# Revit family: 756-106-025 DN150-1200
name_source: partatom
category: Pipe Accessories
units: mm (PartAtom-declared; Revit-internal decimal feet)

## family parameters
Always vertical = Yes
Cut with Voids When Loaded = No
Part Type = Valve - Breaks Into
Round Connector Dimension = Use Diameter
Shared = No
Work Plane-Based = No

## types (29) — shared parameters
1 = 1 mm  [stored 0.00328084 ft]
5 = 5 mm  [stored 0.0164042 ft]
D1 = 6 mm  [stored 0.019685 ft]
D1. = 6 mm  [stored 0.019685 ft]
DN1000_PN10 = 756-1000-1-04006047
 756-1000-1-04006047
 756-1000-1-04006047
756-1000-1-04006047
DN1000_PN16 = 756-1000-1-14006047
DN1200_PN10 = 756-1200-1-04006047
DN1200_PN16 = 756-1200-1-14006047
DN1400_PN10 = 756-1400-1-04006047
DN1400_PN16 = 756-1400-1-14006047
DN150_PN10/16 = 756-0150-1-14006047
DN200_PN10 = 756-0200-1-04006047
DN200_PN16 = 756-0200-1-14006047
 756-0200-1-14006047
756-0200-1-14006047
DN250_PN10 = 756-0250-1-04006047
DN250_PN16 = 756-0250-1-14006047
DN300_PN10 = 756-0300-1-04006047
756-0300-1-14006047
DN300_PN16 = 756-0300-1-14006047
DN350_PN10 = 756-0350-1-04006047
DN350_PN16 = 756-0350-1-14006047
DN400_PN10 = 756-0400-1-04006047
DN400_PN16 = 756-0400-1-14006047
DN450_PN10 = 756-0450-1-04006047
DN450_PN16 = 756-0450-1-14006047
DN500_PN10 = 756-0500-1-04006047
DN500_PN16 = 756-0500-1-14006047
DN600_PN10 = 756-0600-1-04006047
DN600_PN16 = 756-0600-1-14006047
DN700_PN10 = 756-0700-1-04006047
DN700_PN16 = 756-0700-1-14006047
DN800_PN10 = 756-0800-1-04006047
DN800_PN16 = 756-0800-1-14006047
DN900_PN10 = 756-0900-1-04006047
DN900_PN16 = 756-0900-1-14006047
Description_ = AVK DOUBLE ECCENTRIC BUTTERFLY VALVE, PN10/16
Search_table = 756-106-025 DN150-1200
URL product pages = https://www.avkvalves.com
zero-valued in all types: .5, 0, Default Elevation, Stem_dia

## per-type parameters (varying)
- DN0150_PN10/16: Bore=75 mm; DN=150 mm; FL_OD=152 mm; FL_T=19 mm  [stored 0.062336 ft]; H2=200 mm; HW=4 mm  [stored 0.0131234 ft]; Hw=8 mm  [stored 0.0262467 ft]; Inside_R=53 mm; L=105 mm; L1=1 mm  [stored 0.00328084 ft]; L2=1 mm  [stored 0.00328084 ft]; OD=143 mm; Offset=0 mm  [stored 0 ft]; Raised_Dia=106 mm; Raised_dis=3 mm  [stored 0.00984252 ft]; Rib=58 mm; Rib_W=50 mm; Shaft_R=37 mm; W1=155 mm; W2=227 mm; W2_dim1=193 mm; W3=0 mm  [stored 0 ft]; W4=0 mm  [stored 0 ft]; W5=178 mm; W5_dim1=62 mm; W5_dim2=53 mm; W5_dim3=45 mm  [stored 0.147638 ft]; W5_dim4=151 mm; dim1=14 mm  [stored 0.0459318 ft]; disk_T=11 mm; fillet=6 mm  [stored 0.019685 ft]; hand__wheel1=172 mm; shaft1=40 mm  [stored 0.131234 ft]; shaft_dim2=44 mm; shat_T=204 mm; stem=4 mm  [stored 0.0131234 ft]
- DN0200_PN10: Bore=100 mm; DN=200 mm; FL_OD=178 mm; FL_T=20 mm  [stored 0.0656168 ft]; H2=227 mm; HW=4 mm  [stored 0.0131234 ft]; Hw=8 mm  [stored 0.0262467 ft]; Inside_R=70 mm; L=115 mm; L1=1 mm  [stored 0.00328084 ft]; L2=1 mm  [stored 0.00328084 ft]; OD=170 mm; Offset=0 mm  [stored 0 ft]; Raised_Dia=133 mm; Raised_dis=3 mm  [stored 0.00984252 ft]; Rib=63 mm; Rib_W=60 mm; Shaft_R=40 mm  [stored 0.131234 ft]; W1=182 mm; W2=279 mm; W2_dim1=237 mm; W3=0 mm  [stored 0 ft]; W4=0 mm  [stored 0 ft]; W5=178 mm; W5_dim1=62 mm; W5_dim2=53 mm; W5_dim3=45 mm  [stored 0.147638 ft]; W5_dim4=151 mm; dim1=15 mm  [stored 0.0492126 ft]; disk_T=12 mm  [stored 0.0393701 ft]; fillet=6 mm  [stored 0.019685 ft]; hand__wheel1=172 mm; shaft1=44 mm; shaft_dim2=49 mm; shat_T=251 mm; stem=4 mm  [stored 0.0131234 ft]
- DN0200_PN16: Bore=100 mm; DN=200 mm; FL_OD=178 mm; FL_T=20 mm  [stored 0.0656168 ft]; H2=227 mm; HW=4 mm  [stored 0.0131234 ft]; Hw=8 mm  [stored 0.0262467 ft]; Inside_R=70 mm; L=115 mm; L1=1 mm  [stored 0.00328084 ft]; L2=1 mm  [stored 0.00328084 ft]; OD=170 mm; Offset=0 mm  [stored 0 ft]; Raised_Dia=133 mm; Raised_dis=3 mm  [stored 0.00984252 ft]; Rib=63 mm; Rib_W=60 mm; Shaft_R=40 mm  [stored 0.131234 ft]; W1=182 mm; W2=279 mm; W2_dim1=237 mm; W3=0 mm  [stored 0 ft]; W4=0 mm  [stored 0 ft]; W5=178 mm; W5_dim1=62 mm; W5_dim2=53 mm; W5_dim3=45 mm  [stored 0.147638 ft]; W5_dim4=151 mm; dim1=15 mm  [stored 0.0492126 ft]; disk_T=12 mm  [stored 0.0393701 ft]; fillet=6 mm  [stored 0.019685 ft]; hand__wheel1=172 mm; shaft1=44 mm; shaft_dim2=49 mm; shat_T=251 mm; stem=4 mm  [stored 0.0131234 ft]
- DN0250_ PN10: Bore=125 mm; DN=250 mm; FL_OD=211 mm; FL_T=22 mm  [stored 0.0721785 ft]; H2=261 mm; HW=5 mm  [stored 0.0164042 ft]; Hw=9 mm  [stored 0.0295276 ft]; Inside_R=88 mm; L=125 mm; L1=1 mm  [stored 0.00328084 ft]; L2=1 mm  [stored 0.00328084 ft]; OD=198 mm; Offset=0 mm  [stored 0 ft]; Raised_Dia=160 mm; Raised_dis=3 mm  [stored 0.00984252 ft]; Rib=69 mm; Rib_W=69 mm; Shaft_R=44 mm; W1=215 mm; W2=313 mm; W2_dim1=266 mm; W3=0 mm  [stored 0 ft]; W4=3 mm  [stored 0.00984252 ft]; W5=178 mm; W5_dim1=62 mm; W5_dim2=53 mm; W5_dim3=45 mm  [stored 0.147638 ft]; W5_dim4=151 mm; dim1=16 mm  [stored 0.0524934 ft]; disk_T=13 mm  [stored 0.0426509 ft]; fillet=11 mm; hand__wheel1=171 mm; shaft1=48 mm; shaft_dim2=53 mm; shat_T=282 mm; stem=4 mm  [stored 0.0131234 ft]
- DN0250_ PN16: Bore=125 mm; DN=250 mm; FL_OD=211 mm; FL_T=22 mm  [stored 0.0721785 ft]; H2=261 mm; HW=5 mm  [stored 0.0164042 ft]; Hw=9 mm  [stored 0.0295276 ft]; Inside_R=88 mm; L=125 mm; L1=1 mm  [stored 0.00328084 ft]; L2=1 mm  [stored 0.00328084 ft]; OD=198 mm; Offset=0 mm  [stored 0 ft]; Raised_Dia=160 mm; Raised_dis=3 mm  [stored 0.00984252 ft]; Rib=69 mm; Rib_W=69 mm; Shaft_R=44 mm; W1=215 mm; W2=313 mm; W2_dim1=266 mm; W3=0 mm  [stored 0 ft]; W4=3 mm  [stored 0.00984252 ft]; W5=178 mm; W5_dim1=62 mm; W5_dim2=53 mm; W5_dim3=45 mm  [stored 0.147638 ft]; W5_dim4=151 mm; dim1=16 mm  [stored 0.0524934 ft]; disk_T=13 mm  [stored 0.0426509 ft]; fillet=11 mm; hand__wheel1=171 mm; shaft1=48 mm; shaft_dim2=53 mm; shat_T=282 mm; stem=4 mm  [stored 0.0131234 ft]
- DN0300_ PN10: Bore=150 mm; DN=300 mm; FL_OD=237 mm; FL_T=25 mm  [stored 0.082021 ft]; H2=292 mm; HW=5 mm  [stored 0.0164042 ft]; Hw=10 mm  [stored 0.0328084 ft]; Inside_R=105 mm; L=135 mm; L1=1 mm  [stored 0.00328084 ft]; L2=12 mm  [stored 0.0393701 ft]; OD=223 mm; Offset=6 mm  [stored 0.019685 ft]; Raised_Dia=185 mm; Raised_dis=4 mm  [stored 0.0131234 ft]; Rib=74 mm; Rib_W=78 mm; Shaft_R=47 mm; W1=242 mm; W2=343 mm; W2_dim1=292 mm; W3=3 mm  [stored 0.00984252 ft]; W4=52 mm; W5=178 mm; W5_dim1=62 mm; W5_dim2=53 mm; W5_dim3=45 mm  [stored 0.147638 ft]; W5_dim4=151 mm; dim1=19 mm  [stored 0.062336 ft]; disk_T=15 mm  [stored 0.0492126 ft]; fillet=13 mm  [stored 0.0426509 ft]; hand__wheel1=171 mm; shaft1=52 mm; shaft_dim2=57 mm; shat_T=309 mm; stem=5 mm  [stored 0.0164042 ft]
- DN0300_ PN16: Bore=150 mm; DN=300 mm; FL_OD=237 mm; FL_T=25 mm  [stored 0.082021 ft]; H2=292 mm; HW=5 mm  [stored 0.0164042 ft]; Hw=10 mm  [stored 0.0328084 ft]; Inside_R=105 mm; L=135 mm; L1=1 mm  [stored 0.00328084 ft]; L2=12 mm  [stored 0.0393701 ft]; OD=223 mm; Offset=6 mm  [stored 0.019685 ft]; Raised_Dia=185 mm; Raised_dis=4 mm  [stored 0.0131234 ft]; Rib=74 mm; Rib_W=78 mm; Shaft_R=47 mm; W1=242 mm; W2=343 mm; W2_dim1=292 mm; W3=3 mm  [stored 0.00984252 ft]; W4=52 mm; W5=189 mm; W5_dim1=66 mm; W5_dim2=56 mm; W5_dim3=48 mm; W5_dim4=161 mm; dim1=19 mm  [stored 0.062336 ft]; disk_T=15 mm  [stored 0.0492126 ft]; fillet=13 mm  [stored 0.0426509 ft]; hand__wheel1=182 mm; shaft1=52 mm; shaft_dim2=57 mm; shat_T=309 mm; stem=5 mm  [stored 0.0164042 ft]
- DN0350_ PN10: Bore=175 mm; DN=350 mm; FL_OD=267 mm; FL_T=25 mm  [stored 0.082021 ft]; H2=318 mm; HW=5 mm  [stored 0.0164042 ft]; Hw=10 mm  [stored 0.0328084 ft]; Inside_R=123 mm; L=145 mm; L1=20 mm  [stored 0.0656168 ft]; L2=26 mm; OD=253 mm; Offset=3 mm  [stored 0.00984252 ft]; Raised_Dia=215 mm; Raised_dis=4 mm  [stored 0.0131234 ft]; Rib=80 mm; Rib_W=88 mm; Shaft_R=51 mm; W1=272 mm; W2=369 mm; W2_dim1=314 mm; W3=76 mm; W4=87 mm; W5=178 mm; W5_dim1=62 mm; W5_dim2=53 mm; W5_dim3=45 mm  [stored 0.147638 ft]; W5_dim4=151 mm; dim1=19 mm  [stored 0.062336 ft]; disk_T=15 mm  [stored 0.0492126 ft]; fillet=17 mm; hand__wheel1=171 mm; shaft1=56 mm; shaft_dim2=61 mm; shat_T=332 mm; stem=5 mm  [stored 0.0164042 ft]
- DN0350_ PN16: Bore=175 mm; DN=350 mm; FL_OD=267 mm; FL_T=25 mm  [stored 0.082021 ft]; H2=318 mm; HW=5 mm  [stored 0.0164042 ft]; Hw=10 mm  [stored 0.0328084 ft]; Inside_R=123 mm; L=145 mm; L1=20 mm  [stored 0.0656168 ft]; L2=26 mm; OD=253 mm; Offset=3 mm  [stored 0.00984252 ft]; Raised_Dia=215 mm; Raised_dis=4 mm  [stored 0.0131234 ft]; Rib=80 mm; Rib_W=88 mm; Shaft_R=51 mm; W1=272 mm; W2=369 mm; W2_dim1=314 mm; W3=76 mm; W4=87 mm; W5=189 mm; W5_dim1=66 mm; W5_dim2=56 mm; W5_dim3=48 mm; W5_dim4=161 mm; dim1=19 mm  [stored 0.062336 ft]; disk_T=15 mm  [stored 0.0492126 ft]; fillet=17 mm; hand__wheel1=182 mm; shaft1=56 mm; shaft_dim2=61 mm; shat_T=332 mm; stem=5 mm  [stored 0.0164042 ft]
- DN0400_ PN10: Bore=200 mm; DN=400 mm; FL_OD=296 mm; FL_T=25 mm  [stored 0.082021 ft]; H2=349 mm; HW=5 mm  [stored 0.0164042 ft]; Hw=10 mm  [stored 0.0328084 ft]; Inside_R=140 mm; L=155 mm; L1=35 mm  [stored 0.114829 ft]; L2=41 mm  [stored 0.134514 ft]; OD=283 mm; Offset=3 mm  [stored 0.00984252 ft]; Raised_Dia=240 mm; Raised_dis=4 mm  [stored 0.0131234 ft]; Rib=85 mm; Rib_W=99 mm; Shaft_R=54 mm; W1=302 mm; W2=403 mm; W2_dim1=343 mm; W3=108 mm; W4=116 mm; W5=189 mm; W5_dim1=66 mm; W5_dim2=56 mm; W5_dim3=48 mm; W5_dim4=161 mm; dim1=19 mm  [stored 0.062336 ft]; disk_T=15 mm  [stored 0.0492126 ft]; fillet=19 mm  [stored 0.062336 ft]; hand__wheel1=182 mm; shaft1=60 mm; shaft_dim2=66 mm; shat_T=363 mm; stem=5 mm  [stored 0.0164042 ft]
- DN0400_ PN16: Bore=200 mm; DN=400 mm; FL_OD=296 mm; FL_T=25 mm  [stored 0.082021 ft]; H2=349 mm; HW=5 mm  [stored 0.0164042 ft]; Hw=10 mm  [stored 0.0328084 ft]; Inside_R=140 mm; L=155 mm; L1=35 mm  [stored 0.114829 ft]; L2=41 mm  [stored 0.134514 ft]; OD=283 mm; Offset=3 mm  [stored 0.00984252 ft]; Raised_Dia=240 mm; Raised_dis=4 mm  [stored 0.0131234 ft]; Rib=85 mm; Rib_W=99 mm; Shaft_R=54 mm; W1=302 mm; W2=403 mm; W2_dim1=343 mm; W3=108 mm; W4=116 mm; W5=189 mm; W5_dim1=66 mm; W5_dim2=56 mm; W5_dim3=48 mm; W5_dim4=161 mm; dim1=19 mm  [stored 0.062336 ft]; disk_T=15 mm  [stored 0.0492126 ft]; fillet=19 mm  [stored 0.062336 ft]; hand__wheel1=182 mm; shaft1=60 mm; shaft_dim2=66 mm; shat_T=363 mm; stem=5 mm  [stored 0.0164042 ft]
- DN0450_ PN10: Bore=225 mm; DN=450 mm; FL_OD=325 mm; FL_T=26 mm; H2=390 mm; HW=6 mm  [stored 0.019685 ft]; Hw=10 mm  [stored 0.0328084 ft]; Inside_R=158 mm; L=165 mm; L1=48 mm; L2=55 mm; OD=308 mm; Offset=4 mm  [stored 0.0131234 ft]; Raised_Dia=265 mm; Raised_dis=4 mm  [stored 0.0131234 ft]; Rib=91 mm; Rib_W=108 mm; Shaft_R=58 mm; W1=332 mm; W2=440 mm; W2_dim1=374 mm; W3=134 mm; W4=142 mm; W5=189 mm; W5_dim1=66 mm; W5_dim2=56 mm; W5_dim3=48 mm; W5_dim4=161 mm; dim1=19 mm  [stored 0.062336 ft]; disk_T=15 mm  [stored 0.0492126 ft]; fillet=25 mm  [stored 0.082021 ft]; hand__wheel1=181 mm; shaft1=64 mm; shaft_dim2=70 mm; shat_T=396 mm; stem=5 mm  [stored 0.0164042 ft]
- DN0450_ PN16: Bore=225 mm; DN=450 mm; FL_OD=325 mm; FL_T=26 mm; H2=390 mm; HW=6 mm  [stored 0.019685 ft]; Hw=10 mm  [stored 0.0328084 ft]; Inside_R=158 mm; L=165 mm; L1=48 mm; L2=55 mm; OD=308 mm; Offset=4 mm  [stored 0.0131234 ft]; Raised_Dia=274 mm; Raised_dis=4 mm  [stored 0.0131234 ft]; Rib=91 mm; Rib_W=108 mm; Shaft_R=58 mm; W1=332 mm; W2=440 mm; W2_dim1=374 mm; W3=134 mm; W4=142 mm; W5=205 mm; W5_dim1=72 mm; W5_dim2=61 mm; W5_dim3=52 mm; W5_dim4=174 mm; dim1=19 mm  [stored 0.062336 ft]; disk_T=15 mm  [stored 0.0492126 ft]; fillet=25 mm  [stored 0.082021 ft]; hand__wheel1=197 mm; shaft1=64 mm; shaft_dim2=70 mm; shat_T=396 mm; stem=5 mm  [stored 0.0164042 ft]
- DN0500_ PN10: Bore=250 mm; DN=500 mm; FL_OD=331 mm; FL_T=27 mm  [stored 0.0885827 ft]; H2=418 mm; HW=6 mm  [stored 0.019685 ft]; Hw=11 mm; Inside_R=175 mm; L=175 mm; L1=63 mm; L2=69 mm; OD=335 mm; Offset=3 mm  [stored 0.00984252 ft]; Raised_Dia=291 mm; Raised_dis=4 mm  [stored 0.0131234 ft]; Rib=96 mm; Rib_W=117 mm; Shaft_R=61 mm; W1=338 mm; W2=468 mm; W2_dim1=398 mm; W3=161 mm; W4=168 mm; W5=189 mm; W5_dim1=66 mm; W5_dim2=56 mm; W5_dim3=48 mm; W5_dim4=161 mm; dim1=20 mm  [stored 0.0656168 ft]; disk_T=16 mm  [stored 0.0524934 ft]; fillet=29 mm  [stored 0.0951444 ft]; hand__wheel1=181 mm; shaft1=67 mm; shaft_dim2=74 mm; shat_T=421 mm; stem=5 mm  [stored 0.0164042 ft]
- DN0500_ PN16: Bore=250 mm; DN=500 mm; FL_OD=363 mm; FL_T=27 mm  [stored 0.0885827 ft]; H2=427 mm; HW=6 mm  [stored 0.019685 ft]; Hw=11 mm; Inside_R=175 mm; L=175 mm; L1=63 mm; L2=69 mm; OD=335 mm; Offset=3 mm  [stored 0.00984252 ft]; Raised_Dia=305 mm; Raised_dis=4 mm  [stored 0.0131234 ft]; Rib=96 mm; Rib_W=117 mm; Shaft_R=61 mm; W1=370 mm; W2=477 mm; W2_dim1=405 mm; W3=161 mm; W4=168 mm; W5=205 mm; W5_dim1=72 mm; W5_dim2=61 mm; W5_dim3=52 mm; W5_dim4=174 mm; dim1=20 mm  [stored 0.0656168 ft]; disk_T=16 mm  [stored 0.0524934 ft]; fillet=29 mm  [stored 0.0951444 ft]; hand__wheel1=197 mm; shaft1=67 mm; shaft_dim2=74 mm; shat_T=429 mm; stem=5 mm  [stored 0.0164042 ft]
- DN0600_ PN10: Bore=300 mm; DN=600 mm; FL_OD=385 mm; FL_T=30 mm  [stored 0.0984252 ft]; H2=481 mm; HW=7 mm  [stored 0.0229659 ft]; Hw=12 mm  [stored 0.0393701 ft]; Inside_R=210 mm; L=195 mm; L1=94 mm; L2=100 mm; OD=390 mm; Offset=3 mm  [stored 0.00984252 ft]; Raised_Dia=341 mm; Raised_dis=5 mm  [stored 0.0164042 ft]; Rib=107 mm; Rib_W=137 mm; Shaft_R=68 mm; W1=393 mm; W2=536 mm; W2_dim1=456 mm; W3=213 mm; W4=219 mm; W5=205 mm; W5_dim1=72 mm; W5_dim2=61 mm; W5_dim3=52 mm; W5_dim4=174 mm; dim1=23 mm  [stored 0.0754593 ft]; disk_T=18 mm  [stored 0.0590551 ft]; fillet=34 mm; hand__wheel1=196 mm; shaft1=75 mm; shaft_dim2=83 mm; shat_T=482 mm; stem=6 mm  [stored 0.019685 ft]
- DN0600_ PN16: Bore=300 mm; DN=600 mm; FL_OD=426 mm; FL_T=30 mm  [stored 0.0984252 ft]; H2=503 mm; HW=7 mm  [stored 0.0229659 ft]; Hw=12 mm  [stored 0.0393701 ft]; Inside_R=210 mm; L=195 mm; L1=94 mm; L2=100 mm; OD=390 mm; Offset=3 mm  [stored 0.00984252 ft]; Raised_Dia=360 mm; Raised_dis=5 mm  [stored 0.0164042 ft]; Rib=107 mm; Rib_W=137 mm; Shaft_R=68 mm; W1=435 mm; W2=556 mm; W2_dim1=473 mm; W3=213 mm; W4=219 mm; W5=284 mm; W5_dim1=99 mm; W5_dim2=84 mm; W5_dim3=72 mm; W5_dim4=241 mm; dim1=23 mm  [stored 0.0754593 ft]; disk_T=18 mm  [stored 0.0590551 ft]; fillet=34 mm; hand__wheel1=275 mm; shaft1=75 mm; shaft_dim2=83 mm; shat_T=500 mm; stem=6 mm  [stored 0.019685 ft]
- DN0700_ PN10: Bore=350 mm; DN=700 mm; FL_OD=439 mm; FL_T=33 mm; H2=550 mm; HW=7 mm  [stored 0.0229659 ft]; Hw=13 mm  [stored 0.0426509 ft]; Inside_R=245 mm; L=215 mm; L1=127 mm; L2=133 mm; OD=448 mm; Offset=3 mm  [stored 0.00984252 ft]; Raised_Dia=397 mm; Raised_dis=5 mm  [stored 0.0164042 ft]; Rib=118 mm; Rib_W=157 mm; Shaft_R=75 mm; W1=448 mm; W2=641 mm; W2_dim1=545 mm; W3=267 mm; W4=272 mm; W5=396 mm; W5_dim1=139 mm; W5_dim2=118 mm; W5_dim3=100 mm; W5_dim4=337 mm; dim1=25 mm  [stored 0.082021 ft]; disk_T=20 mm  [stored 0.0656168 ft]; fillet=40 mm  [stored 0.131234 ft]; hand__wheel1=386 mm; shaft1=83 mm; shaft_dim2=91 mm; shat_T=577 mm; stem=7 mm  [stored 0.0229659 ft]
- DN0700_ PN16: Bore=350 mm; DN=700 mm; FL_OD=446 mm; FL_T=33 mm; H2=550 mm; HW=7 mm  [stored 0.0229659 ft]; Hw=13 mm  [stored 0.0426509 ft]; Inside_R=245 mm; L=215 mm; L1=127 mm; L2=133 mm; OD=448 mm; Offset=3 mm  [stored 0.00984252 ft]; Raised_Dia=397 mm; Raised_dis=5 mm  [stored 0.0164042 ft]; Rib=118 mm; Rib_W=157 mm; Shaft_R=75 mm; W1=455 mm; W2=641 mm; W2_dim1=545 mm; W3=267 mm; W4=272 mm; W5=517 mm; W5_dim1=181 mm; W5_dim2=154 mm; W5_dim3=131 mm; W5_dim4=439 mm; dim1=25 mm  [stored 0.082021 ft]; disk_T=20 mm  [stored 0.0656168 ft]; fillet=40 mm  [stored 0.131234 ft]; hand__wheel1=507 mm; shaft1=83 mm; shaft_dim2=91 mm; shat_T=577 mm; stem=7 mm  [stored 0.0229659 ft]
- DN0800_ PN10: Bore=400 mm; DN=800 mm; FL_OD=498 mm; FL_T=35 mm  [stored 0.114829 ft]; H2=620 mm; HW=8 mm  [stored 0.0262467 ft]; Hw=14 mm  [stored 0.0459318 ft]; Inside_R=280 mm; L=235 mm; L1=156 mm; L2=162 mm; OD=505 mm; Offset=3 mm  [stored 0.00984252 ft]; Raised_Dia=451 mm; Raised_dis=5 mm  [stored 0.0164042 ft]; Rib=129 mm; Rib_W=177 mm; Shaft_R=82 mm; W1=508 mm; W2=711 mm; W2_dim1=604 mm; W3=314 mm; W4=318 mm; W5=396 mm; W5_dim1=139 mm; W5_dim2=118 mm; W5_dim3=100 mm; W5_dim4=337 mm; dim1=26 mm; disk_T=21 mm  [stored 0.0688976 ft]; fillet=46 mm; hand__wheel1=386 mm; shaft1=90 mm; shaft_dim2=100 mm; shat_T=640 mm; stem=7 mm  [stored 0.0229659 ft]
- DN0800_ PN16: Bore=400 mm; DN=800 mm; FL_OD=503 mm; FL_T=35 mm  [stored 0.114829 ft]; H2=620 mm; HW=8 mm  [stored 0.0262467 ft]; Hw=14 mm  [stored 0.0459318 ft]; Inside_R=280 mm; L=235 mm; L1=156 mm; L2=162 mm; OD=502 mm; Offset=3 mm  [stored 0.00984252 ft]; Raised_Dia=451 mm; Raised_dis=5 mm  [stored 0.0164042 ft]; Rib=129 mm; Rib_W=176 mm; Shaft_R=82 mm; W1=513 mm; W2=711 mm; W2_dim1=604 mm; W3=314 mm; W4=318 mm; W5=517 mm; W5_dim1=181 mm; W5_dim2=154 mm; W5_dim3=131 mm; W5_dim4=439 mm; dim1=26 mm; disk_T=21 mm  [stored 0.0688976 ft]; fillet=46 mm; hand__wheel1=507 mm; shaft1=90 mm; shaft_dim2=100 mm; shat_T=640 mm; stem=7 mm  [stored 0.0229659 ft]
- DN0900_ PN10: Bore=450 mm; DN=900 mm; FL_OD=547 mm; FL_T=38 mm; H2=690 mm; HW=8 mm  [stored 0.0262467 ft]; Hw=15 mm  [stored 0.0492126 ft]; Inside_R=315 mm; L=255 mm; L1=186 mm; L2=192 mm; OD=558 mm; Offset=3 mm  [stored 0.00984252 ft]; Raised_Dia=501 mm; Raised_dis=5 mm  [stored 0.0164042 ft]; Rib=140 mm; Rib_W=195 mm; Shaft_R=89 mm; W1=558 mm; W2=791 mm; W2_dim1=672 mm; W3=361 mm; W4=365 mm; W5=517 mm; W5_dim1=181 mm; W5_dim2=154 mm; W5_dim3=131 mm; W5_dim4=439 mm; dim1=28 mm; disk_T=23 mm  [stored 0.0754593 ft]; fillet=51 mm; hand__wheel1=506 mm; shaft1=98 mm; shaft_dim2=108 mm; shat_T=712 mm; stem=8 mm  [stored 0.0262467 ft]
- DN0900_ PN16: Bore=450 mm; DN=900 mm; FL_OD=552 mm; FL_T=38 mm; H2=690 mm; HW=8 mm  [stored 0.0262467 ft]; Hw=15 mm  [stored 0.0492126 ft]; Inside_R=315 mm; L=255 mm; L1=186 mm; L2=192 mm; OD=558 mm; Offset=3 mm  [stored 0.00984252 ft]; Raised_Dia=501 mm; Raised_dis=5 mm  [stored 0.0164042 ft]; Rib=140 mm; Rib_W=195 mm; Shaft_R=89 mm; W1=563 mm; W2=791 mm; W2_dim1=672 mm; W3=361 mm; W4=365 mm; W5=570 mm; W5_dim1=200 mm; W5_dim2=170 mm; W5_dim3=144 mm; W5_dim4=485 mm; dim1=28 mm; disk_T=23 mm  [stored 0.0754593 ft]; fillet=51 mm; hand__wheel1=559 mm; shaft1=98 mm; shaft_dim2=108 mm; shat_T=712 mm; stem=8 mm  [stored 0.0262467 ft]
- DN1000_ PN10: Bore=500 mm; DN=1000 mm; FL_OD=603 mm; FL_T=40 mm  [stored 0.131234 ft]; H2=770 mm; HW=9 mm  [stored 0.0295276 ft]; Hw=16 mm  [stored 0.0524934 ft]; Inside_R=350 mm; L=275 mm; L1=216 mm; L2=222 mm; OD=613 mm; Offset=3 mm  [stored 0.00984252 ft]; Raised_Dia=556 mm; Raised_dis=5 mm  [stored 0.0164042 ft]; Rib=151 mm; Rib_W=214 mm; Shaft_R=96 mm; W1=615 mm; W2=871 mm; W2_dim1=740 mm; W3=408 mm; W4=412 mm; W5=530 mm; W5_dim1=186 mm; W5_dim2=158 mm; W5_dim3=134 mm; W5_dim4=451 mm; dim1=29 mm  [stored 0.0951444 ft]; disk_T=24 mm  [stored 0.0787402 ft]; fillet=57 mm; hand__wheel1=518 mm; shaft1=106 mm; shaft_dim2=116 mm; shat_T=784 mm; stem=8 mm  [stored 0.0262467 ft]
- DN1000_ PN16: Bore=500 mm; DN=1000 mm; FL_OD=615 mm; FL_T=40 mm  [stored 0.131234 ft]; H2=770 mm; HW=9 mm  [stored 0.0295276 ft]; Hw=16 mm  [stored 0.0524934 ft]; Inside_R=350 mm; L=275 mm; L1=216 mm; L2=222 mm; OD=613 mm; Offset=3 mm  [stored 0.00984252 ft]; Raised_Dia=556 mm; Raised_dis=5 mm  [stored 0.0164042 ft]; Rib=151 mm; Rib_W=214 mm; Shaft_R=96 mm; W1=628 mm; W2=871 mm; W2_dim1=740 mm; W3=408 mm; W4=412 mm; W5=570 mm; W5_dim1=200 mm; W5_dim2=170 mm; W5_dim3=144 mm; W5_dim4=485 mm; dim1=29 mm  [stored 0.0951444 ft]; disk_T=24 mm  [stored 0.0787402 ft]; fillet=57 mm; hand__wheel1=558 mm; shaft1=106 mm; shaft_dim2=116 mm; shat_T=784 mm; stem=8 mm  [stored 0.0262467 ft]
- DN1200_ PN10: Bore=600 mm; DN=1200 mm; FL_OD=713 mm; FL_T=45 mm  [stored 0.147638 ft]; H2=855 mm; HW=10 mm  [stored 0.0328084 ft]; Hw=18 mm  [stored 0.0590551 ft]; Inside_R=420 mm; L=315 mm; L1=269 mm; L2=275 mm; OD=728 mm; Offset=3 mm  [stored 0.00984252 ft]; Raised_Dia=664 mm; Raised_dis=5 mm  [stored 0.0164042 ft]; Rib=173 mm; Rib_W=255 mm; Shaft_R=110 mm; W1=728 mm; W2=956 mm; W2_dim1=813 mm; W3=493 mm; W4=497 mm; W5=570 mm; W5_dim1=200 mm; W5_dim2=170 mm; W5_dim3=144 mm; W5_dim4=485 mm; dim1=32 mm  [stored 0.104987 ft]; disk_T=27 mm  [stored 0.0885827 ft]; fillet=68 mm; hand__wheel1=557 mm; shaft1=121 mm; shaft_dim2=133 mm; shat_T=860 mm; stem=9 mm  [stored 0.0295276 ft]
- DN1200_ PN16: Bore=600 mm; DN=1200 mm; FL_OD=728 mm; FL_T=45 mm  [stored 0.147638 ft]; H2=855 mm; HW=10 mm  [stored 0.0328084 ft]; Hw=18 mm  [stored 0.0590551 ft]; Inside_R=420 mm; L=326 mm; L1=269 mm; L2=275 mm; OD=728 mm; Offset=3 mm  [stored 0.00984252 ft]; Raised_Dia=664 mm; Raised_dis=5 mm  [stored 0.0164042 ft]; Rib=179 mm; Rib_W=255 mm; Shaft_R=114 mm; W1=743 mm; W2=956 mm; W2_dim1=813 mm; W3=493 mm; W4=497 mm; W5=591 mm; W5_dim1=207 mm; W5_dim2=176 mm; W5_dim3=149 mm; W5_dim4=502 mm; dim1=32 mm  [stored 0.104987 ft]; disk_T=27 mm  [stored 0.0885827 ft]; fillet=68 mm; hand__wheel1=578 mm; shaft1=126 mm; shaft_dim2=138 mm; shat_T=860 mm; stem=9 mm  [stored 0.0295276 ft]
- DN1400_ PN10: Bore=700 mm; DN=1400 mm; FL_OD=821 mm; FL_T=46 mm; H2=970 mm; HW=10 mm  [stored 0.0328084 ft]; Hw=18 mm  [stored 0.0590551 ft]; Inside_R=490 mm; L=355 mm; L1=333 mm; L2=339 mm; OD=838 mm; Offset=3 mm  [stored 0.00984252 ft]; Raised_Dia=765 mm; Raised_dis=5 mm  [stored 0.0164042 ft]; Rib=195 mm; Rib_W=293 mm; Shaft_R=124 mm; W1=838 mm; W2=1071 mm; W2_dim1=910 mm; W3=591 mm; W4=595 mm; W5=570 mm; W5_dim1=200 mm; W5_dim2=170 mm; W5_dim3=144 mm; W5_dim4=485 mm; dim1=33 mm; disk_T=28 mm; fillet=80 mm; hand__wheel1=556 mm; shaft1=137 mm; shaft_dim2=150 mm; shat_T=964 mm; stem=9 mm  [stored 0.0295276 ft]
- DN1400_ PN16: Bore=700 mm; DN=1400 mm; FL_OD=826 mm; FL_T=46 mm; H2=970 mm; HW=10 mm  [stored 0.0328084 ft]; Hw=18 mm  [stored 0.0590551 ft]; Inside_R=490 mm; L=355 mm; L1=333 mm; L2=339 mm; OD=838 mm; Offset=3 mm  [stored 0.00984252 ft]; Raised_Dia=765 mm; Raised_dis=5 mm  [stored 0.0164042 ft]; Rib=195 mm; Rib_W=293 mm; Shaft_R=124 mm; W1=843 mm; W2=1119 mm; W2_dim1=951 mm; W3=591 mm; W4=595 mm; W5=591 mm; W5_dim1=207 mm; W5_dim2=176 mm; W5_dim3=149 mm; W5_dim4=502 mm; dim1=33 mm; disk_T=28 mm; fillet=80 mm; hand__wheel1=577 mm; shaft1=137 mm; shaft_dim2=150 mm; shat_T=1007 mm; stem=9 mm  [stored 0.0295276 ft]

note: [stored X ft] marks values corroborated as IEEE doubles in the binary element streams (Revit-internal decimal feet)

## geometry (parser evidence)
native form markers: Sweep x5
no freeform markers — native parametric forms only
